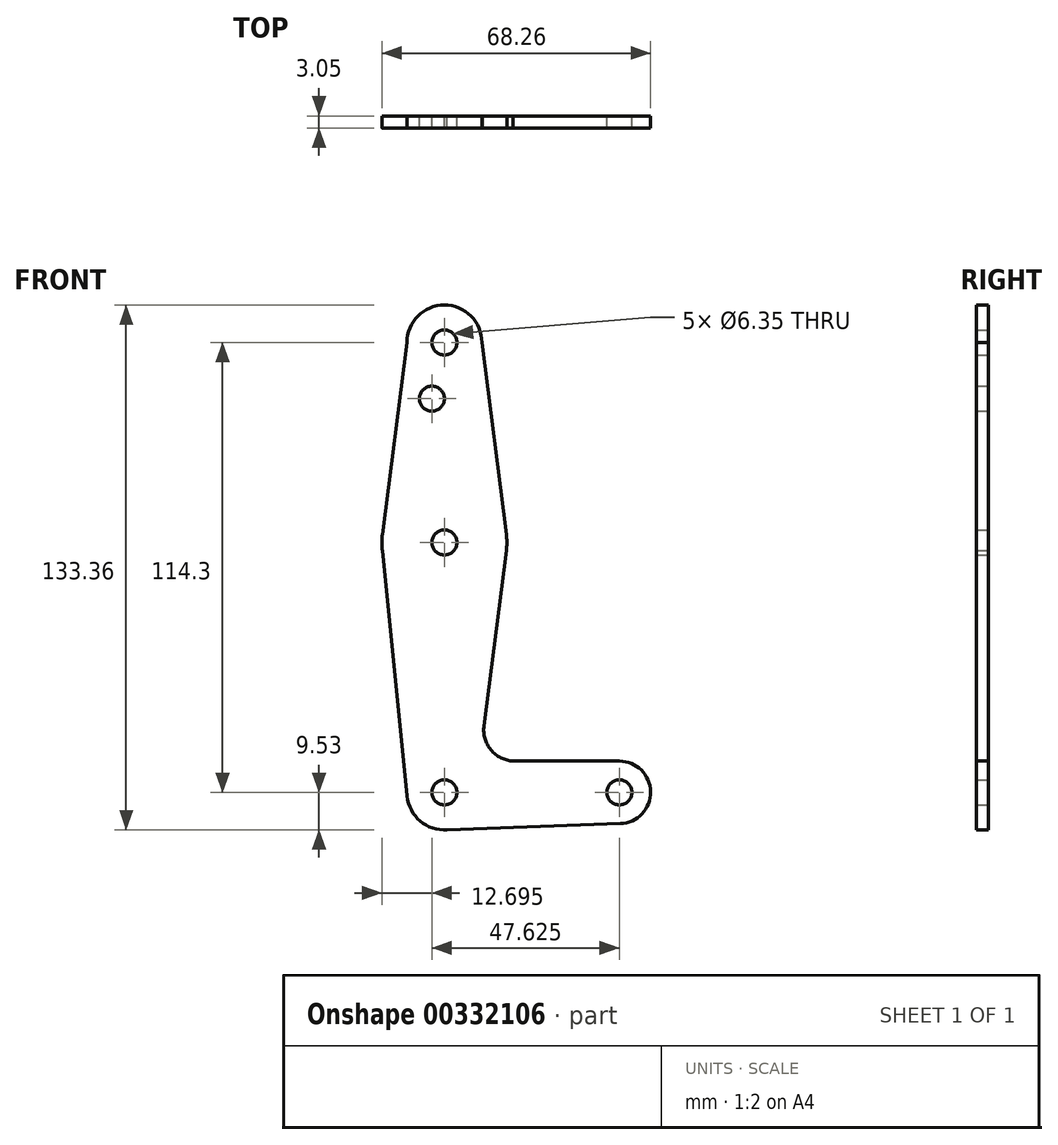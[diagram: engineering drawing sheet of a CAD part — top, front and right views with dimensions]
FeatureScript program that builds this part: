
annotation { "Feature Type Name" : "Feature", "Feature Type Description" : "" }
export const myFeature = defineFeature(function(context is Context, id is Id, definition is map)
    precondition{}
    {
        {
            var Q0;
            Q0=qCreatedBy(makeId("Front.planeOp"),FACE);
            var sketch = newSketch(context, id + "F0", { "sketchPlane" : qUnion([Q0])});
            skLineSegment(sketch, "E0", {"start": v(0, 0) * mm, "end": v(0, 114.3) * mm});
            skLineSegment(sketch, "E1", {"start": v(0, 0) * mm, "end": v(44.45, 0) * mm});
            skCircle(sketch, "E2", {"center": v(0, 114.3) * mm, "radius": 9.53 * mm});
            skCircle(sketch, "E3", {"center": v(0, 0) * mm, "radius": 9.53 * mm});
            skCircle(sketch, "E4", {"center": v(44.45, 0) * mm, "radius": 7.94 * mm});
            skLineSegment(sketch, "E5", {"start": v(0, -9.53) * mm, "end": v(44.73, -7.93) * mm});
            skCircle(sketch, "E6", {"center": v(0, 63.5) * mm, "radius": 15.88 * mm});
            skLineSegment(sketch, "E7", {"start": v(-9.53, 114.3) * mm, "end": v(-15.75, 65.5) * mm});
            skLineSegment(sketch, "E8", {"start": v(9.53, 114.3) * mm, "end": v(15.75, 65.5) * mm});
            skLineSegment(sketch, "E9", {"start": v(10.06, 16.88) * mm, "end": v(15.75, 61.5) * mm});
            skCircle(sketch, "E10", {"center": v(0, 114.3) * mm, "radius": 3.18 * mm});
            skCircle(sketch, "E11", {"center": v(0, 63.5) * mm, "radius": 3.18 * mm});
            skCircle(sketch, "E12", {"center": v(0, 0) * mm, "radius": 3.18 * mm});
            skCircle(sketch, "E13", {"center": v(44.45, 0) * mm, "radius": 3.18 * mm});
            skCircle(sketch, "E14", {"center": v(-3.18, 100.03) * mm, "radius": 3.18 * mm});
            skArc(sketch, "E15.filletArc", {"start": v(10.06, 16.88) * mm, "mid": v(11.83, 10.8) * mm, "end": v(17.48, 7.94) * mm});
            skLineSegment(sketch, "E16", {"start": v(-15.75, 61.5) * mm, "end": v(-9.48, -0.95) * mm});
            skLineSegment(sketch, "E17", {"start": v(17.48, 7.94) * mm, "end": v(44.45, 7.94) * mm});
            skSolve(sketch);
        }
        {
            var Q0;
            Q0 = qSketchRegion(id + "F0", true);
            var Q1;
            {var subQ0=sQuery(id+"F0.wireOp",EDGE,"E12");var subQ1=sQuery(id+"F0.wireOp",EDGE,"E0");var subQ2=makeQuery(id+"F0.imprint","INTERSECT",VERTEX,{"derivedFrom":[subQ1,subQ0]});Q1=makeQuery(id+"F0.imprint","IMPRINT",FACE,{"disambiguationData":[TD([[makeQuery(id+"F0.imprint","IMPRINT",EDGE,{"disambiguationData":[TD([[subQ2,-1.0]])],"derivedFrom":subQ1}),-1.0]])]});}
            extrude(context, id + "F1", {"entities" : qUnion([Q0, Q1]), "depth" : 3.05 * mm});
        }
    });
